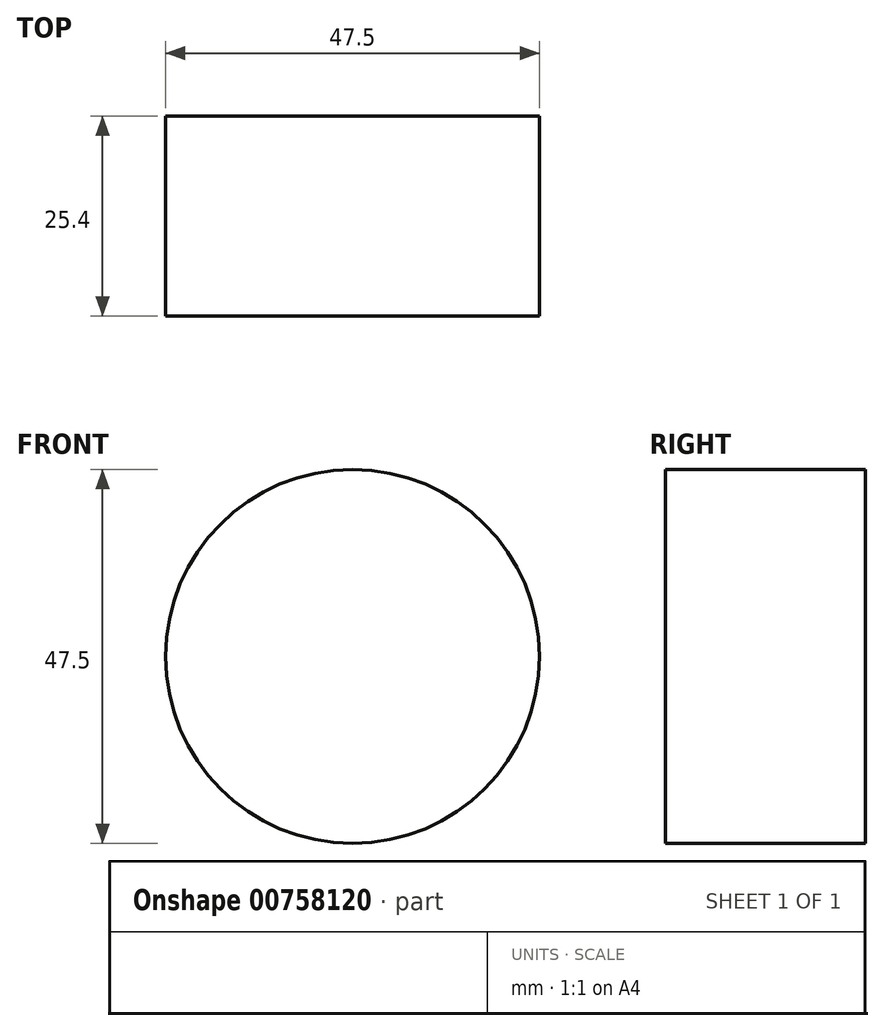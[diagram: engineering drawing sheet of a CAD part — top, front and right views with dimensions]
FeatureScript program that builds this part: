
annotation { "Feature Type Name" : "Feature", "Feature Type Description" : "" }
export const myFeature = defineFeature(function(context is Context, id is Id, definition is map)
    precondition{}
    {
        {
            var Q0;
            Q0=qCreatedBy(makeId("Front.planeOp"),FACE);
            var sketch = newSketch(context, id + "F0", { "sketchPlane" : qUnion([Q0])});
            skCircle(sketch, "E0", {"center": v(0, 0) * mm, "radius": 23.75 * mm});
            skSolve(sketch);
        }
        {
            var Q0;
            Q0=makeQuery(id+"F0.imprint","IMPRINT",FACE,{"disambiguationData":[TD([[makeQuery(id+"F0.imprint","IMPRINT",EDGE,{"derivedFrom":sQuery(id+"F0.wireOp",EDGE,"E0")}),1.0]])]});
            extrude(context, id + "F1", {"entities" : qUnion([Q0]), "depth" : 25.4 * mm, "offsetDistance" : 25.4 * mm});
        }
    });
